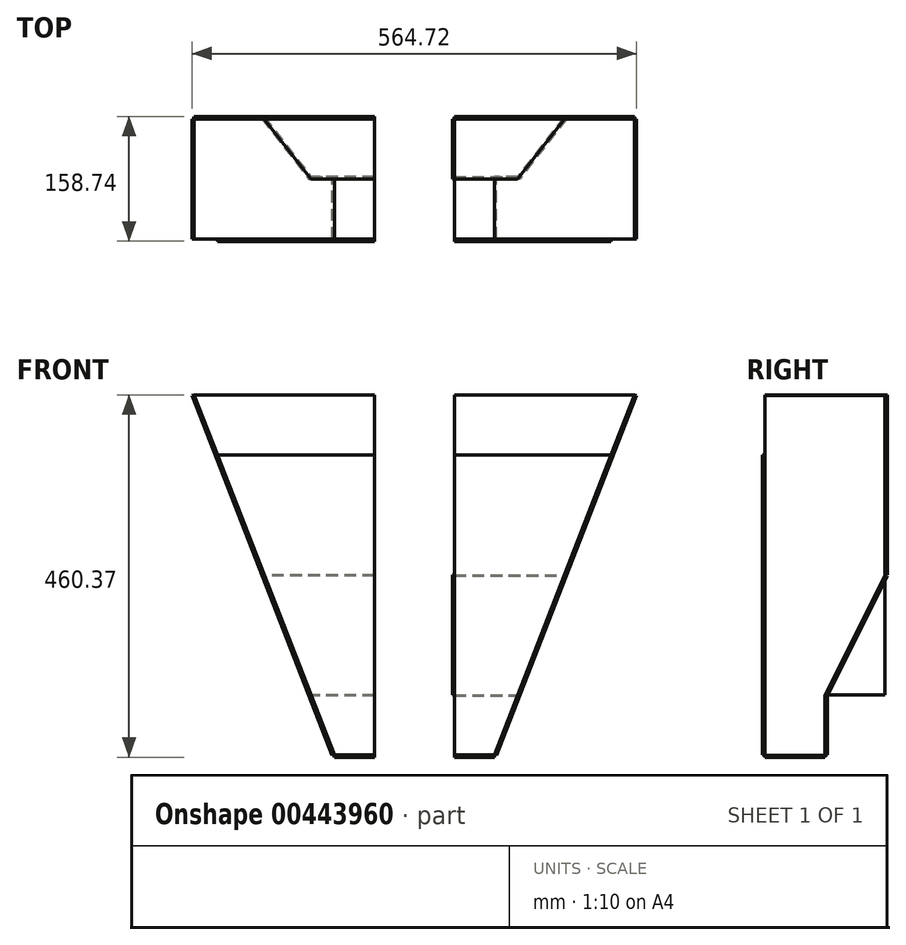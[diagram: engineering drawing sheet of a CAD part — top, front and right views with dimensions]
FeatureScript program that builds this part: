
annotation { "Feature Type Name" : "Feature", "Feature Type Description" : "" }
export const myFeature = defineFeature(function(context is Context, id is Id, definition is map)
    precondition{}
    {
        {
            var Q0;
            Q0=qCreatedBy(makeId("Front.planeOp"),FACE);
            cPlane(context, id + "F0", {"entities" : qUnion([Q0]), "cplaneType" : CPlaneType.OFFSET, "offset" : 152.4 * mm, "width" : 152.4 * mm, "height" : 152.4 * mm});
        }
        {
            var Q0;
            Q0=qCreatedBy(id+"F0.planeOp",FACE);
            var sketch = newSketch(context, id + "F1", { "sketchPlane" : qUnion([Q0])});
            skLineSegment(sketch, "E0", {"start": v(0, 0) * mm, "end": v(50.8, 0) * mm});
            skLineSegment(sketch, "E1", {"start": v(0, 0) * mm, "end": v(0, 381) * mm});
            skLineSegment(sketch, "E2", {"start": v(0, 381) * mm, "end": v(198.97, 381) * mm});
            skLineSegment(sketch, "E3", {"start": v(198.97, 381) * mm, "end": v(50.8, 0) * mm});
            skSolve(sketch);
        }
        {
            var Q0;
            Q0=qCreatedBy(makeId("Front.planeOp"),FACE);
            cPlane(context, id + "F2", {"entities" : qUnion([Q0]), "cplaneType" : CPlaneType.OFFSET, "offset" : 76.2 * mm, "width" : 152.4 * mm, "height" : 152.4 * mm});
        }
        {
            var Q0;
            Q0=qCreatedBy(id+"F2.planeOp",FACE);
            var sketch = newSketch(context, id + "F3", { "sketchPlane" : qUnion([Q0])});
            skLineSegment(sketch, "E4", {"start": v(0, 0) * mm, "end": v(50.8, 0) * mm});
            skLineSegment(sketch, "E5", {"start": v(0, 0) * mm, "end": v(0, 76.2) * mm});
            skLineSegment(sketch, "E6", {"start": v(0, 76.2) * mm, "end": v(80.43, 76.2) * mm});
            skLineSegment(sketch, "E7", {"start": v(80.43, 76.2) * mm, "end": v(50.8, 0) * mm});
            skSolve(sketch);
        }
        {
            var Q0;
            Q0=qCreatedBy(makeId("Front.planeOp"),FACE);
            var sketch = newSketch(context, id + "F4", { "sketchPlane" : qUnion([Q0])});
            skLineSegment(sketch, "E8", {"start": v(0, 0) * mm, "end": v(0, 457.2) * mm, "construction": true});
            skLineSegment(sketch, "E9", {"start": v(0, 457.2) * mm, "end": v(228.6, 457.2) * mm});
            skLineSegment(sketch, "E10", {"start": v(0, 457.2) * mm, "end": v(0, 228.6) * mm});
            skLineSegment(sketch, "E11", {"start": v(0, 228.6) * mm, "end": v(139.7, 228.6) * mm});
            skLineSegment(sketch, "E12", {"start": v(139.7, 228.6) * mm, "end": v(228.6, 457.2) * mm});
            skSolve(sketch);
        }
        {
            var Q0;
            Q0=qCreatedBy(makeId("Right.planeOp"),FACE);
            var sketch = newSketch(context, id + "F5", { "sketchPlane" : qUnion([Q0])});
            skLineSegment(sketch, "E13", {"start": v(0, 0) * mm, "end": v(0, 228.6) * mm});
            skLineSegment(sketch, "E14", {"start": v(0, 228.6) * mm, "end": v(-76.2, 76.2) * mm});
            skLineSegment(sketch, "E15", {"start": v(-76.2, 76.2) * mm, "end": v(-76.2, 0) * mm, "construction": true});
            skLineSegment(sketch, "E16", {"start": v(0, 228.6) * mm, "end": v(0, 76.2) * mm});
            skLineSegment(sketch, "E17", {"start": v(0, 76.2) * mm, "end": v(-76.2, 76.2) * mm});
            skSolve(sketch);
        }
        {
            var Q0;
            Q0=makeQuery(id+"F5.imprint","IMPRINT",FACE,{"disambiguationData":[TD([[makeQuery(id+"F5.imprint","IMPRINT",EDGE,{"derivedFrom":sQuery(id+"F5.wireOp",EDGE,"E14")}),1.0]])]});
            extrude(context, id + "F6", {"entities" : qUnion([Q0]), "oppositeDirection" : true, "depth" : 2.54 * mm});
        }
        {
            var Q0;
            Q0=makeQuery(id+"F6.opExtrude","SWEPT_FACE",FACE,{"disambiguationData":[OSD([sQuery(id+"F5.wireOp",EDGE,"E14")])]});
            var sketch = newSketch(context, id + "F7", { "sketchPlane" : qUnion([Q0])});
            skLineSegment(sketch, "E18", {"start": v(0, 34.08) * mm, "end": v(80.43, 34.08) * mm});
            skLineSegment(sketch, "E19", {"start": v(0, 204.47) * mm, "end": v(139.7, 204.47) * mm});
            skLineSegment(sketch, "E20", {"start": v(0, 204.47) * mm, "end": v(0, 34.08) * mm});
            skLineSegment(sketch, "E21", {"start": v(139.7, 204.47) * mm, "end": v(80.43, 34.08) * mm});
            skSolve(sketch);
        }
        {
            var Q0;
            Q0=makeQuery(id+"F1.imprint","IMPRINT",FACE,{"disambiguationData":[TD([[makeQuery(id+"F1.imprint","IMPRINT",EDGE,{"derivedFrom":sQuery(id+"F1.wireOp",EDGE,"E0")}),1.0]])]});
            extrude(context, id + "F8", {"entities" : qUnion([Q0]), "depth" : 3.17 * mm});
        }
        {
            var Q0;
            Q0=makeQuery(id+"F4.imprint","IMPRINT",FACE,{"disambiguationData":[TD([[makeQuery(id+"F4.imprint","IMPRINT",EDGE,{"derivedFrom":sQuery(id+"F4.wireOp",EDGE,"E9")}),-1.0]])]});
            extrude(context, id + "F9", {"entities" : qUnion([Q0]), "oppositeDirection" : true, "depth" : 3.17 * mm});
        }
        {
            var Q0;
            Q0=makeQuery(id+"F3.imprint","IMPRINT",FACE,{"disambiguationData":[TD([[makeQuery(id+"F3.imprint","IMPRINT",EDGE,{"derivedFrom":sQuery(id+"F3.wireOp",EDGE,"E4")}),1.0]])]});
            extrude(context, id + "F10", {"entities" : qUnion([Q0]), "oppositeDirection" : true, "depth" : 3.17 * mm});
        }
        {
            var Q0;
            Q0=makeQuery(id+"F7.imprint","IMPRINT",FACE,{"disambiguationData":[TD([[makeQuery(id+"F7.imprint","IMPRINT",EDGE,{"derivedFrom":sQuery(id+"F7.wireOp",EDGE,"E18")}),1.0]])]});
            extrude(context, id + "F11", {"entities" : qUnion([Q0]), "oppositeDirection" : true, "depth" : 3.17 * mm});
        }
        {
            var Q0;
            Q0=makeQuery(id+"F8.opExtrude","SWEPT_FACE",FACE,{"disambiguationData":[OSD([sQuery(id+"F1.wireOp",EDGE,"E3")])]});
            var sketch = newSketch(context, id + "F12", { "sketchPlane" : qUnion([Q0])});
            skLineSegment(sketch, "E22", {"start": v(-152.4, 18.41) * mm, "end": v(-76.2, 18.41) * mm});
            skLineSegment(sketch, "E23.0", {"start": v(-76.2, 100.17) * mm, "end": v(-76.2, 18.41) * mm});
            skLineSegment(sketch, "E24.0", {"start": v(0, 263.7) * mm, "end": v(-76.2, 100.17) * mm});
            skLineSegment(sketch, "E25.0", {"start": v(0, 263.7) * mm, "end": v(0, 508.97) * mm});
            skLineSegment(sketch, "E26.0", {"start": v(-152.4, 427.2) * mm, "end": v(-152.4, 18.41) * mm});
            skLineSegment(sketch, "E27", {"start": v(0, 508.97) * mm, "end": v(-152.4, 508.97) * mm});
            skLineSegment(sketch, "E28", {"start": v(-152.4, 508.97) * mm, "end": v(-152.4, 427.2) * mm});
            skSolve(sketch);
        }
        {
            var Q0;
            Q0 = qSketchRegion(id + "F12", true);
            extrude(context, id + "F13", {"entities" : qUnion([Q0]), "depth" : 3.17 * mm});
        }
        {
            var Q0;
            Q0=qCreatedBy(makeId("Right.planeOp"),FACE);
            cPlane(context, id + "F14", {"entities" : qUnion([Q0]), "cplaneType" : CPlaneType.OFFSET, "offset" : 50.8 * mm, "oppositeDirection" : true, "width" : 152.4 * mm, "height" : 152.4 * mm});
        }
        {
            var Q0;
            Q0=makeQuery(id+"F8.opExtrude","SWEPT_FACE",FACE,{"disambiguationData":[OSD([sQuery(id+"F1.wireOp",EDGE,"E0")])]});
            var sketch = newSketch(context, id + "F15", { "sketchPlane" : qUnion([Q0])});
            skLineSegment(sketch, "E29", {"start": v(50.8, 152.4) * mm, "end": v(0, 152.4) * mm});
            skLineSegment(sketch, "E30", {"start": v(0, 152.4) * mm, "end": v(0, 76.2) * mm});
            skLineSegment(sketch, "E31", {"start": v(0, 76.2) * mm, "end": v(50.8, 76.2) * mm});
            skLineSegment(sketch, "E32", {"start": v(50.8, 76.2) * mm, "end": v(50.8, 152.4) * mm});
            skSolve(sketch);
        }
        {
            var Q0;
            Q0 = qSketchRegion(id + "F15", true);
            extrude(context, id + "F16", {"entities" : qUnion([Q0]), "depth" : 3.17 * mm});
        }
        {
            var Q0;
            Q0=makeQuery(id+"F9.opExtrude","SWEPT_BODY",BODY,{"disambiguationData":[OSD([sQuery(id+"F4.wireOp",EDGE,"E9"),sQuery(id+"F4.wireOp",EDGE,"E10"),sQuery(id+"F4.wireOp",EDGE,"E11"),sQuery(id+"F4.wireOp",EDGE,"E12")])]});
            var Q1;
            Q1=makeQuery(id+"F13.opExtrude","SWEPT_BODY",BODY,{"disambiguationData":[OSD([sQuery(id+"F12.wireOp",EDGE,"E22"),sQuery(id+"F12.wireOp",EDGE,"E23.0"),sQuery(id+"F12.wireOp",EDGE,"E24.0"),sQuery(id+"F12.wireOp",EDGE,"E25.0"),sQuery(id+"F12.wireOp",EDGE,"E26.0"),sQuery(id+"F12.wireOp",EDGE,"E27"),sQuery(id+"F12.wireOp",EDGE,"E28")])]});
            var Q2;
            Q2=makeQuery(id+"F8.opExtrude","SWEPT_BODY",BODY,{"disambiguationData":[OSD([sQuery(id+"F1.wireOp",EDGE,"E0"),sQuery(id+"F1.wireOp",EDGE,"E1"),sQuery(id+"F1.wireOp",EDGE,"E2"),sQuery(id+"F1.wireOp",EDGE,"E3")])]});
            var Q3;
            Q3=makeQuery(id+"F10.opExtrude","SWEPT_BODY",BODY,{"disambiguationData":[OSD([sQuery(id+"F3.wireOp",EDGE,"E4"),sQuery(id+"F3.wireOp",EDGE,"E5"),sQuery(id+"F3.wireOp",EDGE,"E6"),sQuery(id+"F3.wireOp",EDGE,"E7")])]});
            var Q4;
            Q4=makeQuery(id+"F16.opExtrude","SWEPT_BODY",BODY,{"disambiguationData":[OSD([sQuery(id+"F15.wireOp",EDGE,"E29"),sQuery(id+"F15.wireOp",EDGE,"E30"),sQuery(id+"F15.wireOp",EDGE,"E31"),sQuery(id+"F15.wireOp",EDGE,"E32")])]});
            var Q5;
            Q5=makeQuery(id+"F11.opExtrude","SWEPT_BODY",BODY,{"disambiguationData":[OSD([sQuery(id+"F7.wireOp",EDGE,"E18"),sQuery(id+"F7.wireOp",EDGE,"E19"),sQuery(id+"F7.wireOp",EDGE,"E20"),sQuery(id+"F7.wireOp",EDGE,"E21")])]});
            var Q6;
            Q6=qCreatedBy(id+"F14.planeOp",FACE);
            mirror(context, id + "F17", {"entities" : qUnion([Q0, Q1, Q2, Q3, Q4, Q5]), "mirrorPlane" : qUnion([Q6])});
        }
    });
